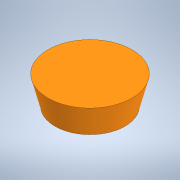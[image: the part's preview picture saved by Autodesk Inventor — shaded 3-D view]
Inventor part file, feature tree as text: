
AUTODESK INVENTOR PART (.ipt)
format: ipt  version: 2020 (Build 240168000, 168)  size: 108,032 bytes
history: native  units: mm
features: revolve x1, sketch x1
ambient origin geometry x8: Origin, YZ Plane, XZ Plane, XY Plane, X Axis, Y Axis, Z Axis, Center Point
bodies: Solid1 (feature_tree)
feature tree (2):
  revolve  "Revolution1"  Angle=90.0deg
  sketch  "Sketch1"  dims[d1=80.0mm d5=90.0deg d8=120.0mm d9=100.0mm]
